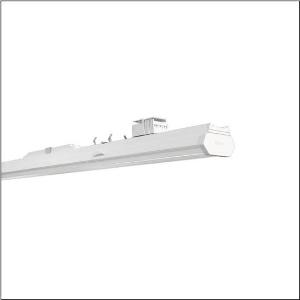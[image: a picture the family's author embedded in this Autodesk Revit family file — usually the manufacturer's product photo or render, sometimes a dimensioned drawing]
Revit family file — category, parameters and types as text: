
# Revit family: licross_r__11_protected_ho_51tp13cn4e5s_b79e
name_source: partatom
category: Lighting Fixtures
units: mm (PartAtom-declared; Revit-internal decimal feet)

## family parameters
Cut with Voids When Loaded = No
Host = Face
Light Source = No
Part Type = Normal
Room Calculation Point = No
Round Connector Dimension = Use Diameter
Shared = No

## types (1)
- --- (1 x LED, 14500 lm, 77.6 W, 4000K)
    Apparent Load = 78 VA
    CIE Flux Codes = 89 96 99 100 99
    Color Rendering = 80
    Color Temperature = 4000K
    Default Elevation = 1800 mm
    Description = Licross® 11 Protected HO, luminaire insert, of sheet steel, galvanised, coil coated, white, length: 1.500mm, width: 90mm, height: 101mm, LED rated luminous flux: 14.500lm, light colour: 840, SDCM (Standard Deviation of Colour Matching)MacAdam ≤ 2 SDCM (initial), control gear: ON/OFF Multilumen, CLOi, with plug, 3-pole, with phase selection, mains connection: 220..240V, AC, 50/60Hz, start of lifetime: 78W, end of service life: 87W, internal wiring halogen-free, primary light control with lens, of plastic, primary optical cover: cover, of PMMA, light emission: direct distribution, primary light characteristic: symmetric, protection rating (complete): IP64, insulation class (complete): insulation class I (protective earthing), certification: CE, ENEC, VDE, UKCA, protection symbol: D if used in an environment with conductive dust loads with corresponding accessories, impact resistance: IK06, permissible ambient temperature for indoor applications: -35..+35°C, corresponds to IFS (International Featured Standards) requirements for safety and quality in the food industry, reducing of maximum allowable ambient temperature of 5°C with ceiling mounting, LABS conformity tested according to VDMA 24364:2018-05, packaging unit: 1 piece
    Height = 92 mm
    Lamp = 1 x LED
    Lamp Light Flux = 14500 lm
    Lamp Power = 77.6 W
    Lamp count = 1
    Length = 1500 mm
    Luminous efficacy = 187 lm/W
    Manufacturer = Siteco
    ModVariant = No
    Model = 51TP13CN4E5S
    Mounting Place = Ceiling
    Mounting Type = Pendant
    Number of Poles = 1
    OnlyDefault = Yes
    Power Factor = 1
    Product Name = Licross® 11 Protected HO
    Product group = luminaire insert | ceiling pendant
    ProductGroupID = 901
    Protection Class = Protection class I
    Protection Degree = IP 64
    RLX_Detail_Level = 1
    RLX_Emergency_Light_Flux = 0 lm
    RLX_Emergency_Type = 0
    RLX_Emergency_Type_DB = No
    RlxData = <blob elided: 22133 chars, md5=ea0527cb>
    Socket = socket
    Standby Power = 0 W
    System Light Flux = 14500 lm
    System Power = 78 W
    Type Comments = factory setting: luminous flux: 100 % | (A | C | E) | 181 mA
    Type Image = l_1256148.jpg
    URL = http://relux.com
    VarID = @adj_093399
    Voltage = 0 V
    Weight = 0.00 kg
    Width = 88 mm

## geometry (parser evidence)
native form markers: Blend x4, Sweep x11
no freeform markers — native parametric forms only
